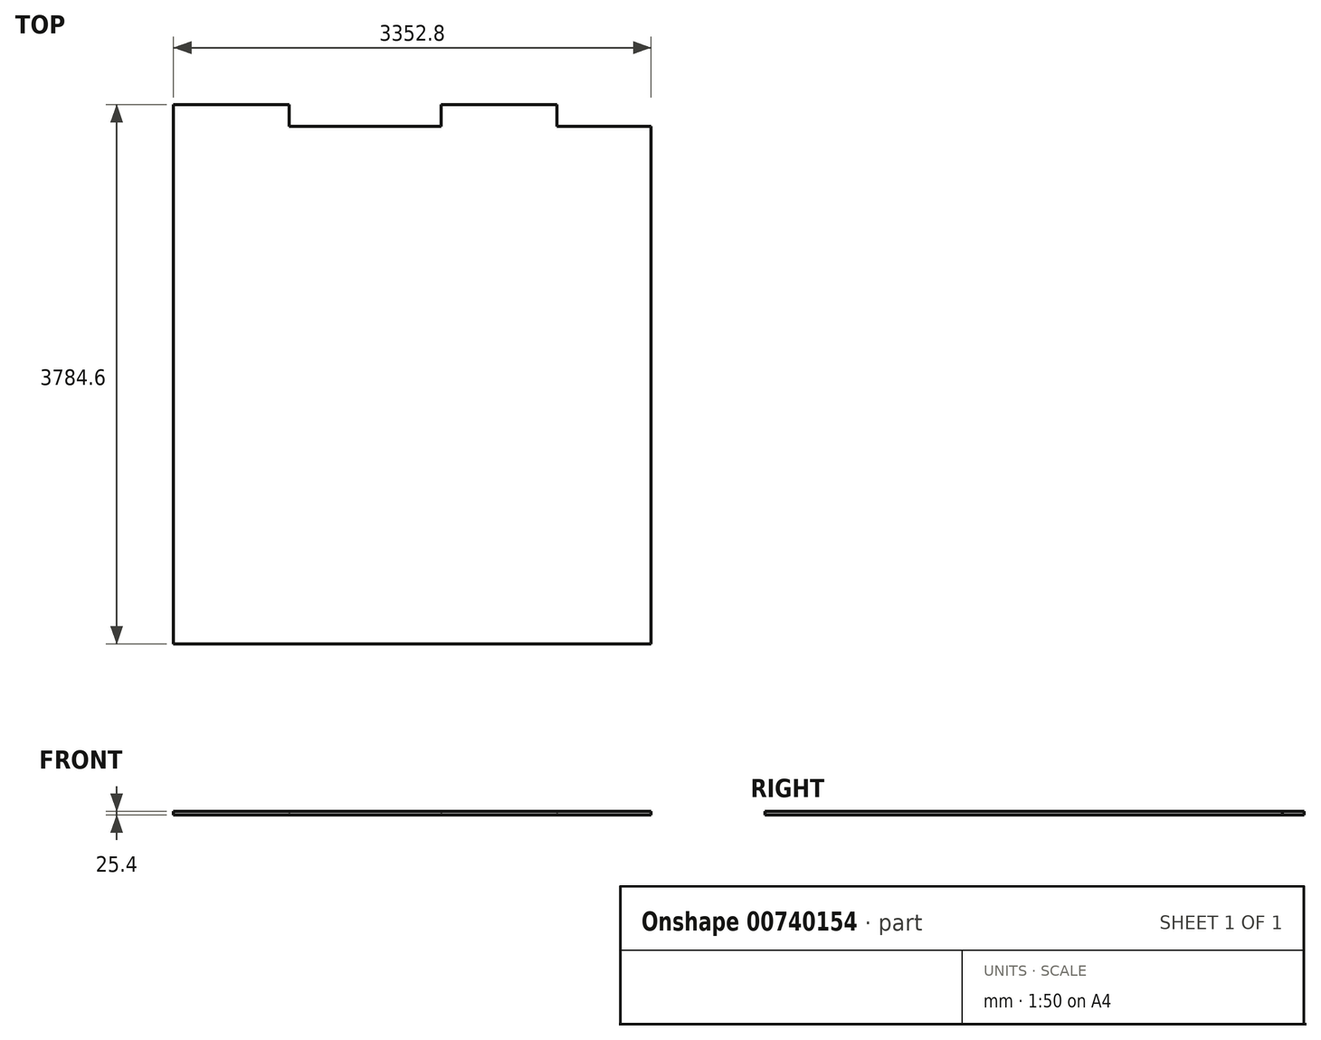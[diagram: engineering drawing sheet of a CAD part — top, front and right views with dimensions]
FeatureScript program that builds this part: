
annotation { "Feature Type Name" : "Feature", "Feature Type Description" : "" }
export const myFeature = defineFeature(function(context is Context, id is Id, definition is map)
    precondition{}
    {
        {
            var Q0;
            Q0=qCreatedBy(makeId("Top.planeOp"),FACE);
            var sketch = newSketch(context, id + "F0", { "sketchPlane" : qUnion([Q0])});
            skLineSegment(sketch, "E0.bottom", {"start": v(-1669.5, 2634.99) * mm, "end": v(1683.3, 2634.99) * mm});
            skLineSegment(sketch, "E0.top", {"start": v(-1669.5, -997.21) * mm, "end": v(1683.3, -997.21) * mm});
            skLineSegment(sketch, "E0.left", {"start": v(-1669.5, 2634.99) * mm, "end": v(-1669.5, -997.21) * mm});
            skLineSegment(sketch, "E0.right", {"start": v(1683.3, 2634.99) * mm, "end": v(1683.3, -997.21) * mm});
            skLineSegment(sketch, "E1.bottom", {"start": v(1022.9, 2634.99) * mm, "end": v(210.1, 2634.99) * mm});
            skLineSegment(sketch, "E1.top", {"start": v(1022.9, 2787.39) * mm, "end": v(210.1, 2787.39) * mm});
            skLineSegment(sketch, "E1.left", {"start": v(1022.9, 2634.99) * mm, "end": v(1022.9, 2787.39) * mm});
            skLineSegment(sketch, "E1.right", {"start": v(210.1, 2634.99) * mm, "end": v(210.1, 2787.39) * mm});
            skLineSegment(sketch, "E2.bottom", {"start": v(-1669.5, 2634.99) * mm, "end": v(-856.7, 2634.99) * mm});
            skLineSegment(sketch, "E2.top", {"start": v(-1669.5, 2787.39) * mm, "end": v(-856.7, 2787.39) * mm});
            skLineSegment(sketch, "E2.left", {"start": v(-1669.5, 2634.99) * mm, "end": v(-1669.5, 2787.39) * mm});
            skLineSegment(sketch, "E2.right", {"start": v(-856.7, 2634.99) * mm, "end": v(-856.7, 2787.39) * mm});
            skSolve(sketch);
        }
        {
            var Q0;
            Q0=makeQuery(id+"F0.imprint","IMPRINT",FACE,{"disambiguationData":[TD([[makeQuery(id+"F0.imprint","IMPRINT",EDGE,{"derivedFrom":sQuery(id+"F0.wireOp",EDGE,"E0.top")}),1.0]])]});
            var Q1;
            Q1=makeQuery(id+"F0.imprint","IMPRINT",FACE,{"disambiguationData":[TD([[makeQuery(id+"F0.imprint","IMPRINT",EDGE,{"derivedFrom":sQuery(id+"F0.wireOp",EDGE,"E2.top")}),-1.0]])]});
            var Q2;
            Q2=makeQuery(id+"F0.imprint","IMPRINT",FACE,{"disambiguationData":[TD([[makeQuery(id+"F0.imprint","IMPRINT",EDGE,{"derivedFrom":sQuery(id+"F0.wireOp",EDGE,"E1.top")}),1.0]])]});
            extrude(context, id + "F1", {"entities" : qUnion([Q0, Q1, Q2]), "depth" : 25.4 * mm, "offsetDistance" : 25.4 * mm});
        }
    });
